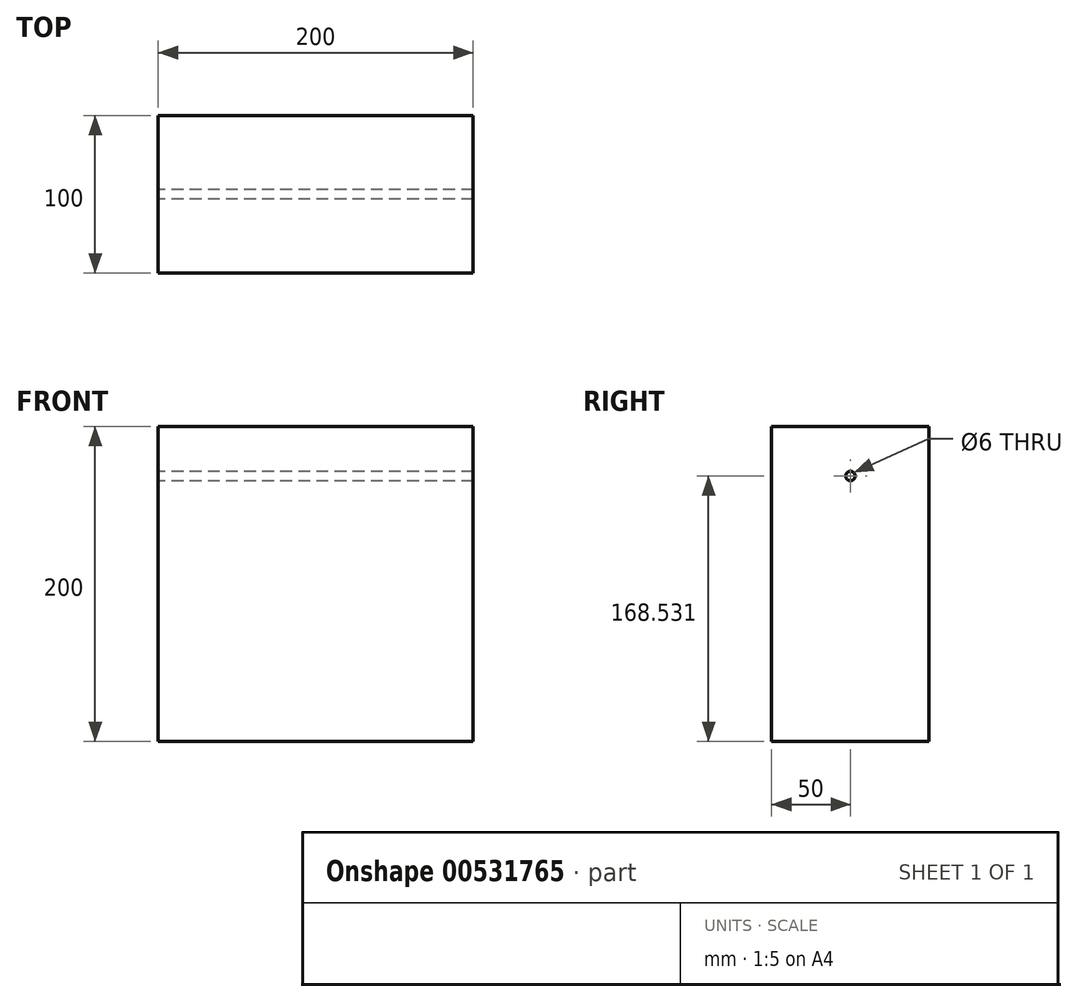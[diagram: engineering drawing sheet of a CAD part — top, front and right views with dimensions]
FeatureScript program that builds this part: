
annotation { "Feature Type Name" : "Feature", "Feature Type Description" : "" }
export const myFeature = defineFeature(function(context is Context, id is Id, definition is map)
    precondition{}
    {
        {
            var Q0;
            Q0=qCreatedBy(makeId("Front.planeOp"),FACE);
            var sketch = newSketch(context, id + "F0", { "sketchPlane" : qUnion([Q0])});
            skLineSegment(sketch, "E0.bottom", {"start": v(-100, 100) * mm, "end": v(100, 100) * mm});
            skLineSegment(sketch, "E0.top", {"start": v(-100, -100) * mm, "end": v(100, -100) * mm});
            skLineSegment(sketch, "E0.left", {"start": v(-100, 100) * mm, "end": v(-100, -100) * mm});
            skLineSegment(sketch, "E0.right", {"start": v(100, 100) * mm, "end": v(100, -100) * mm});
            skPoint(sketch, "E0.middle", {"position": v(0, 0) * mm});
            skSolve(sketch);
        }
        {
            var Q0;
            Q0 = qSketchRegion(id + "F0", true);
            extrude(context, id + "F1", {"entities" : qUnion([Q0]), "depth" : 100 * mm, "offsetDistance" : 25 * mm});
        }
        {
            var Q0;
            Q0=makeQuery(id+"F1.opExtrude","SWEPT_FACE",FACE,{"disambiguationData":[OSD([sQuery(id+"F0.wireOp",EDGE,"E0.left")])]});
            var sketch = newSketch(context, id + "F2", { "sketchPlane" : qUnion([Q0])});
            skLineSegment(sketch, "E1", {"start": v(50, 100) * mm, "end": v(50, -100) * mm, "construction": true});
            skCircle(sketch, "E2", {"center": v(50, 68.53) * mm, "radius": 3 * mm});
            skSolve(sketch);
        }
        {
            var Q0;
            Q0 = qSketchRegion(id + "F2", true);
            extrude(context, id + "F3", {"entities" : qUnion([Q0]), "operationType" : NewBodyOperationType.REMOVE, "oppositeDirection" : true, "depth" : 200 * mm, "offsetDistance" : 25 * mm});
        }
    });
